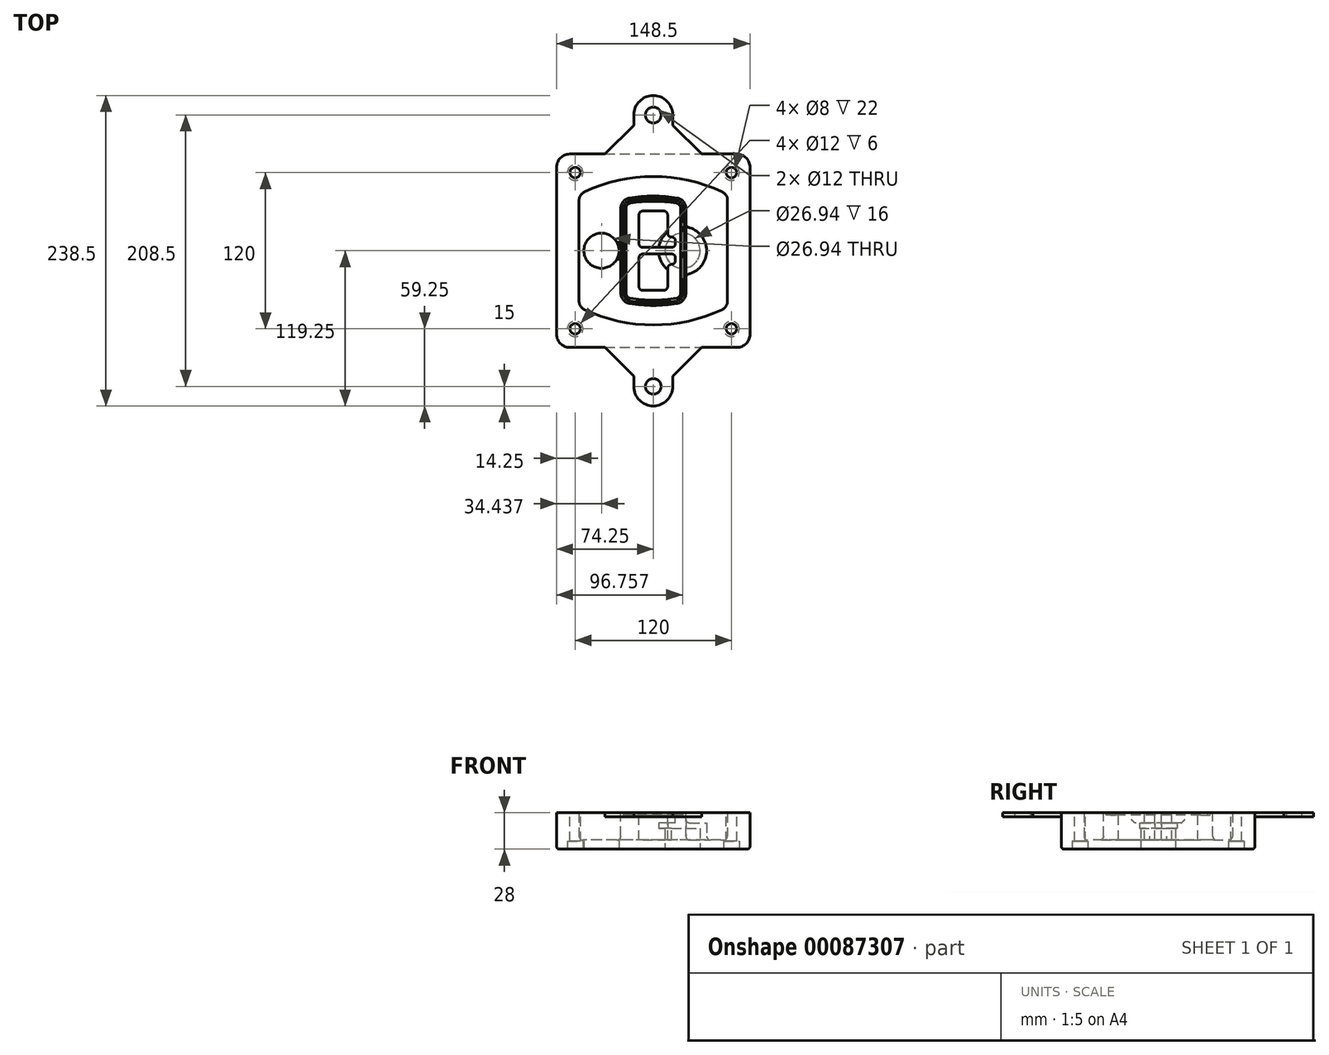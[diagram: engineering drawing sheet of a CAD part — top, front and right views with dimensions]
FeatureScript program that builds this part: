
annotation { "Feature Type Name" : "Feature", "Feature Type Description" : "" }
export const myFeature = defineFeature(function(context is Context, id is Id, definition is map)
    precondition{}
    {
        {
            var Q0;
            Q0=qCreatedBy(makeId("Top.planeOp"),FACE);
            var sketch = newSketch(context, id + "F0", { "sketchPlane" : qUnion([Q0])});
            skPoint(sketch, "E0.rect.middle", {"position": v(0, 0) * mm});
            skLineSegment(sketch, "E1.bottom", {"start": v(-64.25, -74.25) * mm, "end": v(64.25, -74.25) * mm});
            skLineSegment(sketch, "E1.top", {"start": v(-64.25, 74.25) * mm, "end": v(64.25, 74.25) * mm});
            skLineSegment(sketch, "E1.left", {"start": v(-74.25, -64.25) * mm, "end": v(-74.25, 64.25) * mm});
            skLineSegment(sketch, "E1.right", {"start": v(74.25, -64.25) * mm, "end": v(74.25, 64.25) * mm});
            skLineSegment(sketch, "E2", {"start": v(-74.25, 74.25) * mm, "end": v(74.25, -74.25) * mm, "construction": true});
            skLineSegment(sketch, "E3", {"start": v(74.25, 74.25) * mm, "end": v(-74.25, -74.25) * mm, "construction": true});
            skCircle(sketch, "E4", {"center": v(-60, 60) * mm, "radius": 4 * mm});
            skCircle(sketch, "E5", {"center": v(60, 60) * mm, "radius": 4 * mm});
            skCircle(sketch, "E6", {"center": v(60, -60) * mm, "radius": 4 * mm});
            skCircle(sketch, "E7", {"center": v(-60, -60) * mm, "radius": 4 * mm});
            skLineSegment(sketch, "E8", {"start": v(-60, 60) * mm, "end": v(60, 60) * mm, "construction": true});
            skLineSegment(sketch, "E9", {"start": v(60, 60) * mm, "end": v(60, -60) * mm, "construction": true});
            skLineSegment(sketch, "E10", {"start": v(60, -60) * mm, "end": v(-60, -60) * mm, "construction": true});
            skLineSegment(sketch, "E11", {"start": v(-60, -60) * mm, "end": v(-60, 60) * mm, "construction": true});
            skLineSegment(sketch, "E12", {"start": v(-60, 38.83) * mm, "end": v(-60, -38.83) * mm});
            skLineSegment(sketch, "E13", {"start": v(60, 38.83) * mm, "end": v(60, -38.83) * mm});
            skArc(sketch, "E14", {"start": v(54.26, 47.88) * mm, "mid": v(0, 60) * mm, "end": v(-54.26, 47.88) * mm});
            skArc(sketch, "E15", {"start": v(-54.26, -47.88) * mm, "mid": v(0, -60) * mm, "end": v(54.26, -47.88) * mm});
            skLineSegment(sketch, "E16", {"start": v(-60, 0) * mm, "end": v(60, 0) * mm, "construction": true});
            skPoint(sketch, "E17.visualSharp", {"position": v(-60, -45) * mm});
            skArc(sketch, "E17.filletArc", {"start": v(-60, -38.83) * mm, "mid": v(-58.44, -44.2) * mm, "end": v(-54.26, -47.88) * mm});
            skPoint(sketch, "E18.visualSharp", {"position": v(-60, 45) * mm});
            skArc(sketch, "E18.filletArc", {"start": v(-54.26, 47.88) * mm, "mid": v(-58.44, 44.2) * mm, "end": v(-60, 38.83) * mm});
            skPoint(sketch, "E19.visualSharp", {"position": v(60, 45) * mm});
            skArc(sketch, "E19.filletArc", {"start": v(60, 38.83) * mm, "mid": v(58.44, 44.2) * mm, "end": v(54.26, 47.88) * mm});
            skPoint(sketch, "E20.visualSharp", {"position": v(60, -45) * mm});
            skArc(sketch, "E20.filletArc", {"start": v(54.26, -47.88) * mm, "mid": v(58.44, -44.2) * mm, "end": v(60, -38.83) * mm});
            skPoint(sketch, "E21.visualSharp", {"position": v(-74.25, 74.25) * mm});
            skArc(sketch, "E21.filletArc", {"start": v(-64.25, 74.25) * mm, "mid": v(-71.32, 71.32) * mm, "end": v(-74.25, 64.25) * mm});
            skPoint(sketch, "E22.visualSharp", {"position": v(74.25, 74.25) * mm});
            skArc(sketch, "E22.filletArc", {"start": v(74.25, 64.25) * mm, "mid": v(71.32, 71.32) * mm, "end": v(64.25, 74.25) * mm});
            skPoint(sketch, "E23.visualSharp", {"position": v(74.25, -74.25) * mm});
            skArc(sketch, "E23.filletArc", {"start": v(64.25, -74.25) * mm, "mid": v(71.32, -71.32) * mm, "end": v(74.25, -64.25) * mm});
            skPoint(sketch, "E24.visualSharp", {"position": v(-74.25, -74.25) * mm});
            skArc(sketch, "E24.filletArc", {"start": v(-74.25, -64.25) * mm, "mid": v(-71.32, -71.32) * mm, "end": v(-64.25, -74.25) * mm});
            skArc(sketch, "E25.0", {"start": v(57, 38.83) * mm, "mid": v(55.9, 42.58) * mm, "end": v(52.98, 45.17) * mm});
            skLineSegment(sketch, "E25.1", {"start": v(57, 38.83) * mm, "end": v(57, -38.83) * mm});
            skArc(sketch, "E25.2", {"start": v(52.98, -45.17) * mm, "mid": v(55.9, -42.58) * mm, "end": v(57, -38.83) * mm});
            skArc(sketch, "E25.3", {"start": v(-52.98, -45.17) * mm, "mid": v(0, -57) * mm, "end": v(52.98, -45.17) * mm});
            skArc(sketch, "E25.4", {"start": v(-57, -38.83) * mm, "mid": v(-55.9, -42.58) * mm, "end": v(-52.98, -45.17) * mm});
            skArc(sketch, "E25.5", {"start": v(52.98, 45.17) * mm, "mid": v(0, 57) * mm, "end": v(-52.98, 45.17) * mm});
            skLineSegment(sketch, "E25.6", {"start": v(-57, 38.83) * mm, "end": v(-57, -38.83) * mm});
            skArc(sketch, "E25.7", {"start": v(-52.98, 45.17) * mm, "mid": v(-55.9, 42.58) * mm, "end": v(-57, 38.83) * mm});
            skArc(sketch, "E26.0", {"start": v(-55.96, 51.5) * mm, "mid": v(-61.82, 46.33) * mm, "end": v(-64, 38.83) * mm});
            skArc(sketch, "E26.1", {"start": v(55.96, 51.5) * mm, "mid": v(0, 64) * mm, "end": v(-55.96, 51.5) * mm});
            skArc(sketch, "E26.2", {"start": v(64, 38.83) * mm, "mid": v(61.82, 46.33) * mm, "end": v(55.96, 51.5) * mm});
            skLineSegment(sketch, "E26.3", {"start": v(64, 38.83) * mm, "end": v(64, -38.83) * mm});
            skArc(sketch, "E26.4", {"start": v(55.96, -51.5) * mm, "mid": v(61.82, -46.33) * mm, "end": v(64, -38.83) * mm});
            skLineSegment(sketch, "E26.5", {"start": v(-64, 38.83) * mm, "end": v(-64, -38.83) * mm});
            skArc(sketch, "E26.6", {"start": v(-55.96, -51.5) * mm, "mid": v(0, -64) * mm, "end": v(55.96, -51.5) * mm});
            skArc(sketch, "E26.7", {"start": v(-64, -38.83) * mm, "mid": v(-61.82, -46.33) * mm, "end": v(-55.96, -51.5) * mm});
            skSolve(sketch);
        }
        {
            var Q0;
            Q0=makeQuery(id+"F0.imprint","IMPRINT",FACE,{"disambiguationData":[TD([[makeQuery(id+"F0.imprint","IMPRINT",EDGE,{"derivedFrom":sQuery(id+"F0.wireOp",EDGE,"E1.bottom")}),1.0]])]});
            var Q1;
            Q1=makeQuery(id+"F0.imprint","IMPRINT",FACE,{"disambiguationData":[TD([[makeQuery(id+"F0.imprint","IMPRINT",EDGE,{"derivedFrom":sQuery(id+"F0.wireOp",EDGE,"E12")}),1.0]])]});
            var Q2;
            Q2=makeQuery(id+"F0.imprint","IMPRINT",FACE,{"disambiguationData":[TD([[makeQuery(id+"F0.imprint","IMPRINT",EDGE,{"derivedFrom":sQuery(id+"F0.wireOp",EDGE,"E25.0")}),1.0]])]});
            var Q3;
            Q3=makeQuery(id+"F0.imprint","IMPRINT",FACE,{"disambiguationData":[TD([[makeQuery(id+"F0.imprint","IMPRINT",EDGE,{"derivedFrom":sQuery(id+"F0.wireOp",EDGE,"E12")}),-1.0]])]});
            extrude(context, id + "F1", {"entities" : qUnion([Q0, Q1, Q2, Q3]), "oppositeDirection" : true, "depth" : 25 * mm});
        }
        {
            var Q0;
            Q0=makeQuery(id+"F0.imprint","IMPRINT",FACE,{"disambiguationData":[TD([[makeQuery(id+"F0.imprint","IMPRINT",EDGE,{"derivedFrom":sQuery(id+"F0.wireOp",EDGE,"E12")}),1.0]])]});
            extrude(context, id + "F2", {"entities" : qUnion([Q0]), "operationType" : NewBodyOperationType.ADD, "depth" : 3 * mm});
        }
        {
            var Q0;
            Q0=makeQuery(id+"F0.imprint","IMPRINT",FACE,{"disambiguationData":[TD([[makeQuery(id+"F0.imprint","IMPRINT",EDGE,{"derivedFrom":sQuery(id+"F0.wireOp",EDGE,"E25.0")}),1.0]])]});
            extrude(context, id + "F3", {"entities" : qUnion([Q0]), "operationType" : NewBodyOperationType.REMOVE, "oppositeDirection" : true, "depth" : 18 * mm});
        }
        {
            var Q0;
            Q0=makeQuery(id+"F2.opExtrude","CAP_FACE",FACE,{"disambiguationData":[OSD([sQuery(id+"F0.wireOp",EDGE,"E12"),sQuery(id+"F0.wireOp",EDGE,"E13"),sQuery(id+"F0.wireOp",EDGE,"E14"),sQuery(id+"F0.wireOp",EDGE,"E15"),sQuery(id+"F0.wireOp",EDGE,"E17.filletArc"),sQuery(id+"F0.wireOp",EDGE,"E18.filletArc"),sQuery(id+"F0.wireOp",EDGE,"E19.filletArc"),sQuery(id+"F0.wireOp",EDGE,"E20.filletArc"),sQuery(id+"F0.wireOp",EDGE,"E25.0"),sQuery(id+"F0.wireOp",EDGE,"E25.1"),sQuery(id+"F0.wireOp",EDGE,"E25.2"),sQuery(id+"F0.wireOp",EDGE,"E25.3"),sQuery(id+"F0.wireOp",EDGE,"E25.4"),sQuery(id+"F0.wireOp",EDGE,"E25.5"),sQuery(id+"F0.wireOp",EDGE,"E25.6"),sQuery(id+"F0.wireOp",EDGE,"E25.7")])],"isStart":false});
            var sketch = newSketch(context, id + "F4", { "sketchPlane" : qUnion([Q0])});
            skArc(sketch, "E27.0", {"start": v(-18.34, -40.45) * mm, "mid": v(0, -42) * mm, "end": v(18.34, -40.45) * mm});
            skArc(sketch, "E28.0", {"start": v(18.34, 40.45) * mm, "mid": v(0, 42) * mm, "end": v(-18.34, 40.45) * mm});
            skLineSegment(sketch, "E29", {"start": v(-25, 32.57) * mm, "end": v(-25, -32.57) * mm});
            skLineSegment(sketch, "E30", {"start": v(25, 32.57) * mm, "end": v(25, -32.57) * mm});
            skLineSegment(sketch, "E31", {"start": v(-25, 39.1) * mm, "end": v(25, 39.1) * mm, "construction": true});
            skLineSegment(sketch, "E32", {"start": v(-25, -39.1) * mm, "end": v(25, -39.1) * mm, "construction": true});
            skPoint(sketch, "E33.visualSharp", {"position": v(-25, 39.1) * mm});
            skArc(sketch, "E33.filletArc", {"start": v(-18.34, 40.45) * mm, "mid": v(-23.11, 37.73) * mm, "end": v(-25, 32.57) * mm});
            skPoint(sketch, "E34.visualSharp", {"position": v(25, 39.1) * mm});
            skArc(sketch, "E34.filletArc", {"start": v(25, 32.57) * mm, "mid": v(23.11, 37.73) * mm, "end": v(18.34, 40.45) * mm});
            skPoint(sketch, "E35.visualSharp", {"position": v(25, -39.1) * mm});
            skArc(sketch, "E35.filletArc", {"start": v(18.34, -40.45) * mm, "mid": v(23.11, -37.73) * mm, "end": v(25, -32.57) * mm});
            skPoint(sketch, "E36.visualSharp", {"position": v(-25, -39.1) * mm});
            skArc(sketch, "E36.filletArc", {"start": v(-25, -32.57) * mm, "mid": v(-23.11, -37.73) * mm, "end": v(-18.34, -40.45) * mm});
            skArc(sketch, "E37.0", {"start": v(52.98, 45.17) * mm, "mid": v(0, 57) * mm, "end": v(-52.98, 45.17) * mm});
            skArc(sketch, "E37.1", {"start": v(-52.98, 45.17) * mm, "mid": v(-55.9, 42.58) * mm, "end": v(-57, 38.83) * mm});
            skLineSegment(sketch, "E37.2", {"start": v(-57, 38.83) * mm, "end": v(-57, -38.83) * mm});
            skArc(sketch, "E37.3", {"start": v(-57, -38.83) * mm, "mid": v(-55.9, -42.58) * mm, "end": v(-52.98, -45.17) * mm});
            skArc(sketch, "E37.4", {"start": v(-52.98, -45.17) * mm, "mid": v(0, -57) * mm, "end": v(52.98, -45.17) * mm});
            skArc(sketch, "E37.5", {"start": v(52.98, -45.17) * mm, "mid": v(55.9, -42.58) * mm, "end": v(57, -38.83) * mm});
            skLineSegment(sketch, "E37.6", {"start": v(57, 38.83) * mm, "end": v(57, -38.83) * mm});
            skArc(sketch, "E37.7", {"start": v(57, 38.83) * mm, "mid": v(55.9, 42.58) * mm, "end": v(52.98, 45.17) * mm});
            skLineSegment(sketch, "E38.0", {"start": v(23, 32.57) * mm, "end": v(23, -32.57) * mm});
            skArc(sketch, "E38.1", {"start": v(18, -38.48) * mm, "mid": v(21.58, -36.44) * mm, "end": v(23, -32.57) * mm});
            skArc(sketch, "E38.2", {"start": v(-18, -38.48) * mm, "mid": v(0, -40) * mm, "end": v(18, -38.48) * mm});
            skArc(sketch, "E38.3", {"start": v(-23, -32.57) * mm, "mid": v(-21.58, -36.44) * mm, "end": v(-18, -38.48) * mm});
            skLineSegment(sketch, "E38.4", {"start": v(-23, 32.57) * mm, "end": v(-23, -32.57) * mm});
            skArc(sketch, "E38.5", {"start": v(23, 32.57) * mm, "mid": v(21.58, 36.44) * mm, "end": v(18, 38.48) * mm});
            skArc(sketch, "E38.6", {"start": v(-18, 38.48) * mm, "mid": v(-21.58, 36.44) * mm, "end": v(-23, 32.57) * mm});
            skArc(sketch, "E38.7", {"start": v(18, 38.48) * mm, "mid": v(0, 40) * mm, "end": v(-18, 38.48) * mm});
            skArc(sketch, "E39.0", {"start": v(21, 32.57) * mm, "mid": v(20.06, 35.15) * mm, "end": v(17.67, 36.5) * mm});
            skLineSegment(sketch, "E39.1", {"start": v(21, 32.57) * mm, "end": v(21, -32.57) * mm});
            skArc(sketch, "E39.2", {"start": v(17.67, -36.5) * mm, "mid": v(20.06, -35.15) * mm, "end": v(21, -32.57) * mm});
            skArc(sketch, "E39.3", {"start": v(-17.67, -36.5) * mm, "mid": v(0, -38) * mm, "end": v(17.67, -36.5) * mm});
            skArc(sketch, "E39.4", {"start": v(-21, -32.57) * mm, "mid": v(-20.06, -35.15) * mm, "end": v(-17.67, -36.5) * mm});
            skArc(sketch, "E39.5", {"start": v(17.67, 36.5) * mm, "mid": v(0, 38) * mm, "end": v(-17.67, 36.5) * mm});
            skLineSegment(sketch, "E39.6", {"start": v(-21, 32.57) * mm, "end": v(-21, -32.57) * mm});
            skArc(sketch, "E39.7", {"start": v(-17.67, 36.5) * mm, "mid": v(-20.06, 35.15) * mm, "end": v(-21, 32.57) * mm});
            skLineSegment(sketch, "E40", {"start": v(-25, 0) * mm, "end": v(25, 0) * mm, "construction": true});
            skLineSegment(sketch, "E41", {"start": v(-11, 5.5) * mm, "end": v(-11, 27.5) * mm});
            skLineSegment(sketch, "E42", {"start": v(-8, 30.5) * mm, "end": v(8, 30.5) * mm});
            skLineSegment(sketch, "E43", {"start": v(11, 27.5) * mm, "end": v(11, 13.5) * mm});
            skLineSegment(sketch, "E44", {"start": v(14, 10.5) * mm, "end": v(14, 10.5) * mm});
            skLineSegment(sketch, "E45", {"start": v(17, 7.5) * mm, "end": v(17, 5.5) * mm});
            skLineSegment(sketch, "E46", {"start": v(14, 2.5) * mm, "end": v(-8, 2.5) * mm});
            skPoint(sketch, "E47.visualSharp", {"position": v(-11, 30.5) * mm});
            skArc(sketch, "E47.filletArc", {"start": v(-8, 30.5) * mm, "mid": v(-10.12, 29.62) * mm, "end": v(-11, 27.5) * mm});
            skPoint(sketch, "E48.visualSharp", {"position": v(11, 30.5) * mm});
            skArc(sketch, "E48.filletArc", {"start": v(11, 27.5) * mm, "mid": v(10.12, 29.62) * mm, "end": v(8, 30.5) * mm});
            skPoint(sketch, "E49.visualSharp", {"position": v(11, 10.5) * mm});
            skArc(sketch, "E49.filletArc", {"start": v(11, 13.5) * mm, "mid": v(11.88, 11.38) * mm, "end": v(14, 10.5) * mm});
            skPoint(sketch, "E50.visualSharp", {"position": v(17, 10.5) * mm});
            skArc(sketch, "E50.filletArc", {"start": v(17, 7.5) * mm, "mid": v(16.12, 9.62) * mm, "end": v(14, 10.5) * mm});
            skPoint(sketch, "E51.visualSharp", {"position": v(17, 2.5) * mm});
            skArc(sketch, "E51.filletArc", {"start": v(14, 2.5) * mm, "mid": v(16.12, 3.38) * mm, "end": v(17, 5.5) * mm});
            skPoint(sketch, "E52.visualSharp", {"position": v(-11, 2.5) * mm});
            skArc(sketch, "E52.filletArc", {"start": v(-11, 5.5) * mm, "mid": v(-10.12, 3.38) * mm, "end": v(-8, 2.5) * mm});
            skLineSegment(sketch, "E53.0.MirrorCS", {"start": v(14, -2.5) * mm, "end": v(-8, -2.5) * mm});
            skArc(sketch, "E54.0.MirrorCS", {"start": v(-11, -5.5) * mm, "mid": v(-10.12, -3.38) * mm, "end": v(-8, -2.5) * mm});
            skLineSegment(sketch, "E55.0.MirrorCS", {"start": v(-11, -5.5) * mm, "end": v(-11, -27.5) * mm});
            skArc(sketch, "E56.0.MirrorCS", {"start": v(-8, -30.5) * mm, "mid": v(-10.12, -29.62) * mm, "end": v(-11, -27.5) * mm});
            skLineSegment(sketch, "E57.0.MirrorCS", {"start": v(-8, -30.5) * mm, "end": v(8, -30.5) * mm});
            skArc(sketch, "E58.0.MirrorCS", {"start": v(11, -27.5) * mm, "mid": v(10.12, -29.62) * mm, "end": v(8, -30.5) * mm});
            skLineSegment(sketch, "E59.0.MirrorCS", {"start": v(11, -27.5) * mm, "end": v(11, -13.5) * mm});
            skArc(sketch, "E60.0.MirrorCS", {"start": v(11, -13.5) * mm, "mid": v(11.88, -11.38) * mm, "end": v(14, -10.5) * mm});
            skArc(sketch, "E61.0.MirrorCS", {"start": v(17, -7.5) * mm, "mid": v(16.12, -9.62) * mm, "end": v(14, -10.5) * mm});
            skLineSegment(sketch, "E62.0.MirrorCS", {"start": v(17, -7.5) * mm, "end": v(17, -5.5) * mm});
            skArc(sketch, "E63.0.MirrorCS", {"start": v(14, -2.5) * mm, "mid": v(16.12, -3.38) * mm, "end": v(17, -5.5) * mm});
            skSolve(sketch);
        }
        {
            var Q0;
            Q0=makeQuery(id+"F4.imprint","IMPRINT",FACE,{"disambiguationData":[TD([[makeQuery(id+"F4.imprint","IMPRINT",EDGE,{"derivedFrom":sQuery(id+"F4.wireOp",EDGE,"E27.0")}),1.0]])]});
            var Q1;
            Q1=makeQuery(id+"F4.imprint","IMPRINT",FACE,{"disambiguationData":[TD([[makeQuery(id+"F4.imprint","IMPRINT",EDGE,{"derivedFrom":sQuery(id+"F4.wireOp",EDGE,"E38.0")}),-1.0]])]});
            var Q2;
            Q2=makeQuery(id+"F4.imprint","IMPRINT",FACE,{"disambiguationData":[TD([[makeQuery(id+"F4.imprint","IMPRINT",EDGE,{"derivedFrom":sQuery(id+"F4.wireOp",EDGE,"E39.0")}),1.0]])]});
            extrude(context, id + "F5", {"entities" : qUnion([Q0, Q1, Q2]), "operationType" : NewBodyOperationType.ADD, "endBound" : BoundingType.UP_TO_NEXT, "oppositeDirection" : true, "depth" : 25 * mm});
        }
        {
            var Q0;
            Q0=makeQuery(id+"F4.imprint","IMPRINT",FACE,{"disambiguationData":[TD([[makeQuery(id+"F4.imprint","IMPRINT",EDGE,{"derivedFrom":sQuery(id+"F4.wireOp",EDGE,"E38.0")}),-1.0]])]});
            extrude(context, id + "F6", {"entities" : qUnion([Q0]), "operationType" : NewBodyOperationType.REMOVE, "oppositeDirection" : true, "depth" : 2 * mm});
        }
        {
            var Q0;
            Q0=makeQuery(id+"F1.opExtrude","CAP_FACE",FACE,{"disambiguationData":[OSD([sQuery(id+"F0.wireOp",EDGE,"E1.bottom"),sQuery(id+"F0.wireOp",EDGE,"E1.top"),sQuery(id+"F0.wireOp",EDGE,"E1.left"),sQuery(id+"F0.wireOp",EDGE,"E1.right"),sQuery(id+"F0.wireOp",EDGE,"E4"),sQuery(id+"F0.wireOp",EDGE,"E5"),sQuery(id+"F0.wireOp",EDGE,"E6"),sQuery(id+"F0.wireOp",EDGE,"E7"),sQuery(id+"F0.wireOp",EDGE,"E21.filletArc"),sQuery(id+"F0.wireOp",EDGE,"E22.filletArc"),sQuery(id+"F0.wireOp",EDGE,"E23.filletArc"),sQuery(id+"F0.wireOp",EDGE,"E24.filletArc")])],"isStart":false});
            var sketch = newSketch(context, id + "F7", { "sketchPlane" : qUnion([Q0])});
            skCircle(sketch, "E64", {"center": v(22.5, 0) * mm, "radius": 13.47 * mm});
            skCircle(sketch, "E65", {"center": v(-39.81, 0) * mm, "radius": 13.47 * mm});
            skLineSegment(sketch, "E66", {"start": v(74.25, 0) * mm, "end": v(-74.25, 0) * mm});
            skCircle(sketch, "E67", {"center": v(22.5, 0) * mm, "radius": 18.47 * mm});
            skCircle(sketch, "E68", {"center": v(60, -60) * mm, "radius": 6 * mm});
            skCircle(sketch, "E69", {"center": v(-60, -60) * mm, "radius": 6 * mm});
            skCircle(sketch, "E70", {"center": v(-60, 60) * mm, "radius": 6 * mm});
            skCircle(sketch, "E71", {"center": v(60, 60) * mm, "radius": 6 * mm});
            skSolve(sketch);
        }
        {
            var Q0;
            {var subQ1=sQuery(id+"F7.wireOp",EDGE,"E66");var subQ4=sQuery(id+"F7.wireOp",EDGE,"E64");var subQ6=makeQuery(id+"F7.imprint","INTERSECT",VERTEX,{"disambiguationData":[OD(0.0)],"derivedFrom":[subQ4,subQ1]});Q0=makeQuery(id+"F7.imprint","IMPRINT",FACE,{"disambiguationData":[TD([[makeQuery(id+"F7.imprint","IMPRINT",EDGE,{"disambiguationData":[TD([[subQ6,-1.0]])],"derivedFrom":subQ4}),-1.0]])]});}
            var Q1;
            {var subQ0=sQuery(id+"F7.wireOp",EDGE,"E66");var subQ1=sQuery(id+"F7.wireOp",EDGE,"E64");var subQ3=makeQuery(id+"F7.imprint","INTERSECT",VERTEX,{"disambiguationData":[OD(0.0)],"derivedFrom":[subQ1,subQ0]});Q1=makeQuery(id+"F7.imprint","IMPRINT",FACE,{"disambiguationData":[TD([[makeQuery(id+"F7.imprint","IMPRINT",EDGE,{"disambiguationData":[TD([[subQ3,-1.0]])],"derivedFrom":subQ1}),1.0]])]});}
            var Q2;
            {var subQ0=sQuery(id+"F7.wireOp",EDGE,"E66");var subQ1=sQuery(id+"F7.wireOp",EDGE,"E64");var subQ3=makeQuery(id+"F7.imprint","INTERSECT",VERTEX,{"disambiguationData":[OD(0.0)],"derivedFrom":[subQ1,subQ0]});Q2=makeQuery(id+"F7.imprint","IMPRINT",FACE,{"disambiguationData":[TD([[makeQuery(id+"F7.imprint","IMPRINT",EDGE,{"disambiguationData":[TD([[subQ3,1.0]])],"derivedFrom":subQ1}),1.0]])]});}
            var Q3;
            {var subQ1=sQuery(id+"F7.wireOp",EDGE,"E66");var subQ4=sQuery(id+"F7.wireOp",EDGE,"E64");var subQ6=makeQuery(id+"F7.imprint","INTERSECT",VERTEX,{"disambiguationData":[OD(0.0)],"derivedFrom":[subQ4,subQ1]});Q3=makeQuery(id+"F7.imprint","IMPRINT",FACE,{"disambiguationData":[TD([[makeQuery(id+"F7.imprint","IMPRINT",EDGE,{"disambiguationData":[TD([[subQ6,1.0]])],"derivedFrom":subQ4}),-1.0]])]});}
            extrude(context, id + "F8", {"entities" : qUnion([Q0, Q1, Q2, Q3]), "operationType" : NewBodyOperationType.ADD, "oppositeDirection" : true, "depth" : 20 * mm});
        }
        {
            var Q0;
            {var subQ0=sQuery(id+"F7.wireOp",EDGE,"E66");var subQ1=sQuery(id+"F7.wireOp",EDGE,"E64");var subQ3=makeQuery(id+"F7.imprint","INTERSECT",VERTEX,{"disambiguationData":[OD(0.0)],"derivedFrom":[subQ1,subQ0]});Q0=makeQuery(id+"F7.imprint","IMPRINT",FACE,{"disambiguationData":[TD([[makeQuery(id+"F7.imprint","IMPRINT",EDGE,{"disambiguationData":[TD([[subQ3,-1.0]])],"derivedFrom":subQ1}),1.0]])]});}
            var Q1;
            {var subQ0=sQuery(id+"F7.wireOp",EDGE,"E66");var subQ1=sQuery(id+"F7.wireOp",EDGE,"E64");var subQ3=makeQuery(id+"F7.imprint","INTERSECT",VERTEX,{"disambiguationData":[OD(0.0)],"derivedFrom":[subQ1,subQ0]});Q1=makeQuery(id+"F7.imprint","IMPRINT",FACE,{"disambiguationData":[TD([[makeQuery(id+"F7.imprint","IMPRINT",EDGE,{"disambiguationData":[TD([[subQ3,1.0]])],"derivedFrom":subQ1}),1.0]])]});}
            extrude(context, id + "F9", {"entities" : qUnion([Q0, Q1]), "operationType" : NewBodyOperationType.REMOVE, "oppositeDirection" : true, "depth" : 16 * mm});
        }
        {
            var Q0;
            {var subQ0=sQuery(id+"F7.wireOp",EDGE,"E66");var subQ1=sQuery(id+"F7.wireOp",EDGE,"E65");var subQ3=makeQuery(id+"F7.imprint","INTERSECT",VERTEX,{"disambiguationData":[OD(0.0)],"derivedFrom":[subQ1,subQ0]});Q0=makeQuery(id+"F7.imprint","IMPRINT",FACE,{"disambiguationData":[TD([[makeQuery(id+"F7.imprint","IMPRINT",EDGE,{"disambiguationData":[TD([[subQ3,-1.0]])],"derivedFrom":subQ1}),1.0]])]});}
            var Q1;
            {var subQ0=sQuery(id+"F7.wireOp",EDGE,"E66");var subQ1=sQuery(id+"F7.wireOp",EDGE,"E65");var subQ3=makeQuery(id+"F7.imprint","INTERSECT",VERTEX,{"disambiguationData":[OD(0.0)],"derivedFrom":[subQ1,subQ0]});Q1=makeQuery(id+"F7.imprint","IMPRINT",FACE,{"disambiguationData":[TD([[makeQuery(id+"F7.imprint","IMPRINT",EDGE,{"disambiguationData":[TD([[subQ3,1.0]])],"derivedFrom":subQ1}),1.0]])]});}
            extrude(context, id + "F10", {"entities" : qUnion([Q0, Q1]), "operationType" : NewBodyOperationType.REMOVE, "oppositeDirection" : true, "depth" : 25 * mm});
        }
        {
            var Q0;
            Q0=makeQuery(id+"F7.imprint","IMPRINT",FACE,{"disambiguationData":[TD([[makeQuery(id+"F7.imprint","IMPRINT",EDGE,{"derivedFrom":sQuery(id+"F7.wireOp",EDGE,"E68")}),1.0]])]});
            var Q1;
            Q1=makeQuery(id+"F7.imprint","IMPRINT",FACE,{"disambiguationData":[TD([[makeQuery(id+"F7.imprint","IMPRINT",EDGE,{"derivedFrom":makeQuery(id+"F1.opExtrude","CAP_EDGE",EDGE,{"disambiguationData":[OSD([sQuery(id+"F0.wireOp",EDGE,"E5")])],"isStart":false})}),-1.0]])]});
            var Q2;
            Q2=makeQuery(id+"F7.imprint","IMPRINT",FACE,{"disambiguationData":[TD([[makeQuery(id+"F7.imprint","IMPRINT",EDGE,{"derivedFrom":sQuery(id+"F7.wireOp",EDGE,"E69")}),1.0]])]});
            var Q3;
            Q3=makeQuery(id+"F7.imprint","IMPRINT",FACE,{"disambiguationData":[TD([[makeQuery(id+"F7.imprint","IMPRINT",EDGE,{"derivedFrom":makeQuery(id+"F1.opExtrude","CAP_EDGE",EDGE,{"disambiguationData":[OSD([sQuery(id+"F0.wireOp",EDGE,"E4")])],"isStart":false})}),-1.0]])]});
            var Q4;
            Q4=makeQuery(id+"F7.imprint","IMPRINT",FACE,{"disambiguationData":[TD([[makeQuery(id+"F7.imprint","IMPRINT",EDGE,{"derivedFrom":sQuery(id+"F7.wireOp",EDGE,"E70")}),1.0]])]});
            var Q5;
            Q5=makeQuery(id+"F7.imprint","IMPRINT",FACE,{"disambiguationData":[TD([[makeQuery(id+"F7.imprint","IMPRINT",EDGE,{"derivedFrom":makeQuery(id+"F1.opExtrude","CAP_EDGE",EDGE,{"disambiguationData":[OSD([sQuery(id+"F0.wireOp",EDGE,"E7")])],"isStart":false})}),-1.0]])]});
            var Q6;
            Q6=makeQuery(id+"F7.imprint","IMPRINT",FACE,{"disambiguationData":[TD([[makeQuery(id+"F7.imprint","IMPRINT",EDGE,{"derivedFrom":sQuery(id+"F7.wireOp",EDGE,"E71")}),1.0]])]});
            var Q7;
            Q7=makeQuery(id+"F7.imprint","IMPRINT",FACE,{"disambiguationData":[TD([[makeQuery(id+"F7.imprint","IMPRINT",EDGE,{"derivedFrom":makeQuery(id+"F1.opExtrude","CAP_EDGE",EDGE,{"disambiguationData":[OSD([sQuery(id+"F0.wireOp",EDGE,"E6")])],"isStart":false})}),-1.0]])]});
            extrude(context, id + "F11", {"entities" : qUnion([Q0, Q1, Q2, Q3, Q4, Q5, Q6, Q7]), "operationType" : NewBodyOperationType.REMOVE, "oppositeDirection" : true, "depth" : 6 * mm});
        }
        {
            var Q0;
            Q0=makeQuery(id+"F9.boolean.opBoolean","COPY",FACE,{"derivedFrom":makeQuery(id+"F9.opExtrude","CAP_FACE",FACE,{"disambiguationData":[OSD([sQuery(id+"F7.wireOp",EDGE,"E64")])],"isStart":false})});
            var sketch = newSketch(context, id + "F12", { "sketchPlane" : qUnion([Q0])});
            skArc(sketch, "E72.0", {"start": v(11, 14.45) * mm, "mid": v(6.45, 9.13) * mm, "end": v(4.2, 2.5) * mm});
            skArc(sketch, "E72.1", {"start": v(4.2, -2.5) * mm, "mid": v(6.45, -9.13) * mm, "end": v(11, -14.45) * mm});
            skLineSegment(sketch, "E73", {"start": v(4.2, -2.5) * mm, "end": v(14, -2.5) * mm});
            skLineSegment(sketch, "E74.0", {"start": v(14, 2.5) * mm, "end": v(4.2, 2.5) * mm});
            skArc(sketch, "E74.1", {"start": v(14, 2.5) * mm, "mid": v(16.12, 3.38) * mm, "end": v(17, 5.5) * mm});
            skLineSegment(sketch, "E74.2", {"start": v(17, 7.5) * mm, "end": v(17, 5.5) * mm});
            skArc(sketch, "E74.3", {"start": v(17, 7.5) * mm, "mid": v(16.12, 9.62) * mm, "end": v(14, 10.5) * mm});
            skArc(sketch, "E74.4", {"start": v(11, 13.5) * mm, "mid": v(11.88, 11.38) * mm, "end": v(14, 10.5) * mm});
            skLineSegment(sketch, "E74.5", {"start": v(11, 14.45) * mm, "end": v(11, 13.5) * mm});
            skLineSegment(sketch, "E74.7", {"start": v(14, -2.5) * mm, "end": v(4.2, -2.5) * mm});
            skArc(sketch, "E74.8", {"start": v(14, -2.5) * mm, "mid": v(16.12, -3.38) * mm, "end": v(17, -5.5) * mm});
            skLineSegment(sketch, "E74.9", {"start": v(17, -7.5) * mm, "end": v(17, -5.5) * mm});
            skArc(sketch, "E74.10", {"start": v(17, -7.5) * mm, "mid": v(16.12, -9.62) * mm, "end": v(14, -10.5) * mm});
            skArc(sketch, "E74.11", {"start": v(11, -13.5) * mm, "mid": v(11.88, -11.38) * mm, "end": v(14, -10.5) * mm});
            skLineSegment(sketch, "E74.12", {"start": v(11, -14.45) * mm, "end": v(11, -13.5) * mm});
            skPoint(sketch, "E75.orphan", {"position": v(11, -27.5) * mm});
            skPoint(sketch, "E76.orphan", {"position": v(-8, -2.5) * mm});
            skPoint(sketch, "E77.orphan", {"position": v(-8, 2.5) * mm});
            skPoint(sketch, "E78.orphan", {"position": v(11, 27.5) * mm});
            skSolve(sketch);
        }
        {
            var Q0;
            {var subQ7=sQuery(id+"F12.wireOp",EDGE,"E72.0");var subQ14=sQuery(id+"F12.wireOp",EDGE,"E72.1");var subQ16=sQuery(id+"F12.wireOp",EDGE,"E74.1");var subQ18=sQuery(id+"F12.wireOp",EDGE,"E74.8");Q0=qUnion([makeQuery(id+"F12.imprint","IMPRINT",FACE,{"disambiguationData":[TD([[makeQuery(id+"F12.imprint","IMPRINT",EDGE,{"derivedFrom":subQ7}),1.0]])]}),makeQuery(id+"F12.imprint","IMPRINT",FACE,{"disambiguationData":[TD([[makeQuery(id+"F12.imprint","IMPRINT",EDGE,{"derivedFrom":subQ14}),1.0]])]}),makeQuery(id+"F12.imprint","IMPRINT",FACE,{"disambiguationData":[TD([[makeQuery(id+"F12.imprint","IMPRINT",EDGE,{"derivedFrom":subQ16}),1.0]])]}),makeQuery(id+"F12.imprint","IMPRINT",FACE,{"disambiguationData":[TD([[makeQuery(id+"F12.imprint","IMPRINT",EDGE,{"derivedFrom":subQ18}),-1.0]])]})]);}
            var Q1;
            Q1=makeQuery(id+"F5.boolean.opBoolean","SPLIT",FACE,{"disambiguationData":[TD([makeQuery(id+"F5.opExtrude","SWEPT_FACE",FACE,{"disambiguationData":[OSD([sQuery(id+"F4.wireOp",EDGE,"E41")])]})])],"derivedFrom":makeQuery(id+"F3.boolean.opBoolean","COPY",FACE,{"derivedFrom":makeQuery(id+"F3.opExtrude","CAP_FACE",FACE,{"disambiguationData":[OSD([sQuery(id+"F0.wireOp",EDGE,"E25.0"),sQuery(id+"F0.wireOp",EDGE,"E25.1"),sQuery(id+"F0.wireOp",EDGE,"E25.2"),sQuery(id+"F0.wireOp",EDGE,"E25.3"),sQuery(id+"F0.wireOp",EDGE,"E25.4"),sQuery(id+"F0.wireOp",EDGE,"E25.5"),sQuery(id+"F0.wireOp",EDGE,"E25.6"),sQuery(id+"F0.wireOp",EDGE,"E25.7")])],"isStart":false})})});
            extrude(context, id + "F13", {"entities" : qUnion([Q0]), "operationType" : NewBodyOperationType.REMOVE, "endBound" : BoundingType.UP_TO_SURFACE, "endBoundEntityFace" : qUnion([Q1]), "depth" : 25 * mm});
        }
        {
            var Q0;
            Q0=makeQuery(id+"F3.boolean.opBoolean","COPY",EDGE,{"derivedFrom":makeQuery(id+"F3.opExtrude","CAP_EDGE",EDGE,{"disambiguationData":[OSD([sQuery(id+"F0.wireOp",EDGE,"E25.6")])],"isStart":false})});
            var Q1;
            Q1=makeQuery(id+"F8.boolean.opBoolean","INTERSECT",EDGE,{"derivedFrom":[makeQuery(id+"F5.opExtrude","SWEPT_FACE",FACE,{"disambiguationData":[OSD([sQuery(id+"F4.wireOp",EDGE,"E30")])]}),makeQuery(id+"F8.opExtrude","CAP_FACE",FACE,{"disambiguationData":[OSD([sQuery(id+"F7.wireOp",EDGE,"E67")])],"isStart":false})]});
            var Q2;
            Q2=makeQuery(id+"F8.boolean.opBoolean","INTERSECT",EDGE,{"disambiguationData":[OD(1.0)],"derivedFrom":[makeQuery(id+"F5.opExtrude","SWEPT_FACE",FACE,{"disambiguationData":[OSD([sQuery(id+"F4.wireOp",EDGE,"E30")])]}),makeQuery(id+"F8.opExtrude","SWEPT_FACE",FACE,{"disambiguationData":[OSD([sQuery(id+"F7.wireOp",EDGE,"E67")])]})]});
            var Q3;
            {var subQ0=sQuery(id+"F4.wireOp",EDGE,"E30");Q3=makeQuery(id+"F8.boolean.opBoolean","SPLIT",EDGE,{"disambiguationData":[TD([makeQuery(id+"F5.opExtrude","SWEPT_FACE",FACE,{"disambiguationData":[OSD([sQuery(id+"F4.wireOp",EDGE,"E35.filletArc")])]})])],"derivedFrom":makeQuery(id+"F5.opExtrude","CAP_EDGE",EDGE,{"disambiguationData":[OSD([subQ0])],"isStart":false})});}
            var Q4;
            {var subQ0=sQuery(id+"F0.wireOp",EDGE,"E25.7");var subQ1=sQuery(id+"F0.wireOp",EDGE,"E25.1");var subQ2=sQuery(id+"F0.wireOp",EDGE,"E25.6");var subQ3=sQuery(id+"F0.wireOp",EDGE,"E25.5");var subQ4=sQuery(id+"F0.wireOp",EDGE,"E25.4");var subQ5=sQuery(id+"F0.wireOp",EDGE,"E25.0");var subQ6=sQuery(id+"F0.wireOp",EDGE,"E25.2");var subQ7=sQuery(id+"F0.wireOp",EDGE,"E25.3");Q4=makeQuery(id+"F8.boolean.opBoolean","INTERSECT",EDGE,{"derivedFrom":[makeQuery(id+"F5.boolean.opBoolean","SPLIT",FACE,{"disambiguationData":[TD([makeQuery(id+"F2.opExtrude","SWEPT_FACE",FACE,{"disambiguationData":[OSD([subQ5])]})])],"derivedFrom":makeQuery(id+"F3.boolean.opBoolean","COPY",FACE,{"derivedFrom":makeQuery(id+"F3.opExtrude","CAP_FACE",FACE,{"disambiguationData":[OSD([subQ5,subQ1,subQ6,subQ7,subQ4,subQ3,subQ2,subQ0])],"isStart":false})})}),makeQuery(id+"F8.opExtrude","SWEPT_FACE",FACE,{"disambiguationData":[OSD([sQuery(id+"F7.wireOp",EDGE,"E67")])]})]});}
            var Q5;
            Q5=makeQuery(id+"F8.boolean.opBoolean","INTERSECT",EDGE,{"disambiguationData":[OD(0.0)],"derivedFrom":[makeQuery(id+"F5.opExtrude","SWEPT_FACE",FACE,{"disambiguationData":[OSD([sQuery(id+"F4.wireOp",EDGE,"E30")])]}),makeQuery(id+"F8.opExtrude","SWEPT_FACE",FACE,{"disambiguationData":[OSD([sQuery(id+"F7.wireOp",EDGE,"E67")])]})]});
            fillet(context, id + "F14", {"entities" : qUnion([Q0, Q1, Q2, Q3, Q4, Q5]), "radius" : 3 * mm, "tangentPropagation" : true, "allowEdgeOverflow" : false});
        }
        {
            var Q0;
            Q0=makeQuery(id+"F1.opExtrude","CAP_EDGE",EDGE,{"disambiguationData":[OSD([sQuery(id+"F0.wireOp",EDGE,"E1.bottom")])],"isStart":false});
            fillet(context, id + "F15", {"entities" : qUnion([Q0]), "radius" : 2 * mm, "tangentPropagation" : true, "allowEdgeOverflow" : false});
        }
        {
            var Q0;
            {var subQ0=sQuery(id+"F0.wireOp",EDGE,"E22.filletArc");var subQ1=sQuery(id+"F0.wireOp",EDGE,"E7");var subQ2=sQuery(id+"F0.wireOp",EDGE,"E6");var subQ3=sQuery(id+"F0.wireOp",EDGE,"E5");var subQ4=sQuery(id+"F0.wireOp",EDGE,"E4");var subQ5=sQuery(id+"F0.wireOp",EDGE,"E1.bottom");var subQ6=sQuery(id+"F0.wireOp",EDGE,"E21.filletArc");var subQ7=sQuery(id+"F0.wireOp",EDGE,"E1.top");var subQ8=sQuery(id+"F0.wireOp",EDGE,"E1.left");var subQ9=sQuery(id+"F0.wireOp",EDGE,"E1.right");var subQ10=sQuery(id+"F0.wireOp",EDGE,"E23.filletArc");var subQ11=sQuery(id+"F0.wireOp",EDGE,"E24.filletArc");Q0=makeQuery(id+"F2.boolean.opBoolean","SPLIT",FACE,{"disambiguationData":[TD([makeQuery(id+"F1.opExtrude","SWEPT_FACE",FACE,{"disambiguationData":[OSD([subQ5])]})])],"derivedFrom":makeQuery(id+"F1.opExtrude","CAP_FACE",FACE,{"disambiguationData":[OSD([subQ5,subQ7,subQ8,subQ9,subQ4,subQ3,subQ2,subQ1,subQ6,subQ0,subQ10,subQ11])],"isStart":true})});}
            var sketch = newSketch(context, id + "F16", { "sketchPlane" : qUnion([Q0])});
            skLineSegment(sketch, "E79", {"start": v(0, 74.25) * mm, "end": v(0, 104.25) * mm, "construction": true});
            skCircle(sketch, "E80", {"center": v(0, 104.25) * mm, "radius": 6 * mm});
            skArc(sketch, "E81", {"start": v(15, 104.25) * mm, "mid": v(0, 119.25) * mm, "end": v(-15, 104.25) * mm});
            skLineSegment(sketch, "E82", {"start": v(-15, 104.25) * mm, "end": v(-15, 96.36) * mm});
            skLineSegment(sketch, "E83", {"start": v(15, 104.25) * mm, "end": v(15, 96.36) * mm});
            skLineSegment(sketch, "E84", {"start": v(-15, 96.36) * mm, "end": v(-37.11, 74.25) * mm});
            skLineSegment(sketch, "E85", {"start": v(15, 96.36) * mm, "end": v(37.11, 74.25) * mm});
            skLineSegment(sketch, "E86", {"start": v(74.25, 0) * mm, "end": v(167.19, 0) * mm, "construction": true});
            skArc(sketch, "E87.MirrorCS", {"start": v(-15, 104.25) * mm, "mid": v(0, 119.25) * mm, "end": v(15, 104.25) * mm});
            skArc(sketch, "E88.MirrorCS", {"start": v(-15, -104.25) * mm, "mid": v(0, -119.25) * mm, "end": v(15, -104.25) * mm});
            skLineSegment(sketch, "E89.MirrorCS", {"start": v(15, -96.36) * mm, "end": v(37.11, -74.25) * mm});
            skLineSegment(sketch, "E90.MirrorCS", {"start": v(-15, -96.36) * mm, "end": v(-37.11, -74.25) * mm});
            skLineSegment(sketch, "E91.MirrorCS", {"start": v(0, -74.25) * mm, "end": v(0, -104.25) * mm, "construction": true});
            skCircle(sketch, "E92.MirrorC", {"center": v(0, -104.25) * mm, "radius": 6 * mm});
            skLineSegment(sketch, "E93.MirrorCS", {"start": v(15, -104.25) * mm, "end": v(15, -96.36) * mm});
            skLineSegment(sketch, "E94.MirrorCS", {"start": v(-15, -104.25) * mm, "end": v(-15, -96.36) * mm});
            skSolve(sketch);
        }
        {
            var Q0;
            Q0=makeQuery(id+"F16.imprint","IMPRINT",FACE,{"disambiguationData":[TD([[makeQuery(id+"F16.imprint","IMPRINT",EDGE,{"derivedFrom":sQuery(id+"F16.wireOp",EDGE,"E83")}),-1.0]])]});
            var Q1;
            Q1=makeQuery(id+"F16.imprint","IMPRINT",FACE,{"disambiguationData":[TD([[makeQuery(id+"F16.imprint","IMPRINT",EDGE,{"derivedFrom":makeQuery(id+"F1.opExtrude","CAP_EDGE",EDGE,{"disambiguationData":[OSD([sQuery(id+"F0.wireOp",EDGE,"E1.left")])],"isStart":true})}),-1.0]])]});
            var Q2;
            Q2=makeQuery(id+"F16.imprint","IMPRINT",FACE,{"disambiguationData":[TD([[makeQuery(id+"F16.imprint","IMPRINT",EDGE,{"derivedFrom":sQuery(id+"F16.wireOp",EDGE,"E88.MirrorCS")}),1.0]])]});
            var Q3;
            Q3=makeQuery(id+"F2.opExtrude","CAP_FACE",FACE,{"disambiguationData":[OSD([sQuery(id+"F0.wireOp",EDGE,"E12"),sQuery(id+"F0.wireOp",EDGE,"E13"),sQuery(id+"F0.wireOp",EDGE,"E14"),sQuery(id+"F0.wireOp",EDGE,"E15"),sQuery(id+"F0.wireOp",EDGE,"E17.filletArc"),sQuery(id+"F0.wireOp",EDGE,"E18.filletArc"),sQuery(id+"F0.wireOp",EDGE,"E19.filletArc"),sQuery(id+"F0.wireOp",EDGE,"E20.filletArc"),sQuery(id+"F0.wireOp",EDGE,"E25.0"),sQuery(id+"F0.wireOp",EDGE,"E25.1"),sQuery(id+"F0.wireOp",EDGE,"E25.2"),sQuery(id+"F0.wireOp",EDGE,"E25.3"),sQuery(id+"F0.wireOp",EDGE,"E25.4"),sQuery(id+"F0.wireOp",EDGE,"E25.5"),sQuery(id+"F0.wireOp",EDGE,"E25.6"),sQuery(id+"F0.wireOp",EDGE,"E25.7")])],"isStart":false});
            extrude(context, id + "F17", {"entities" : qUnion([Q0, Q1, Q2]), "operationType" : NewBodyOperationType.ADD, "endBound" : BoundingType.UP_TO_SURFACE, "endBoundEntityFace" : qUnion([Q3]), "depth" : 25 * mm});
        }
    });
